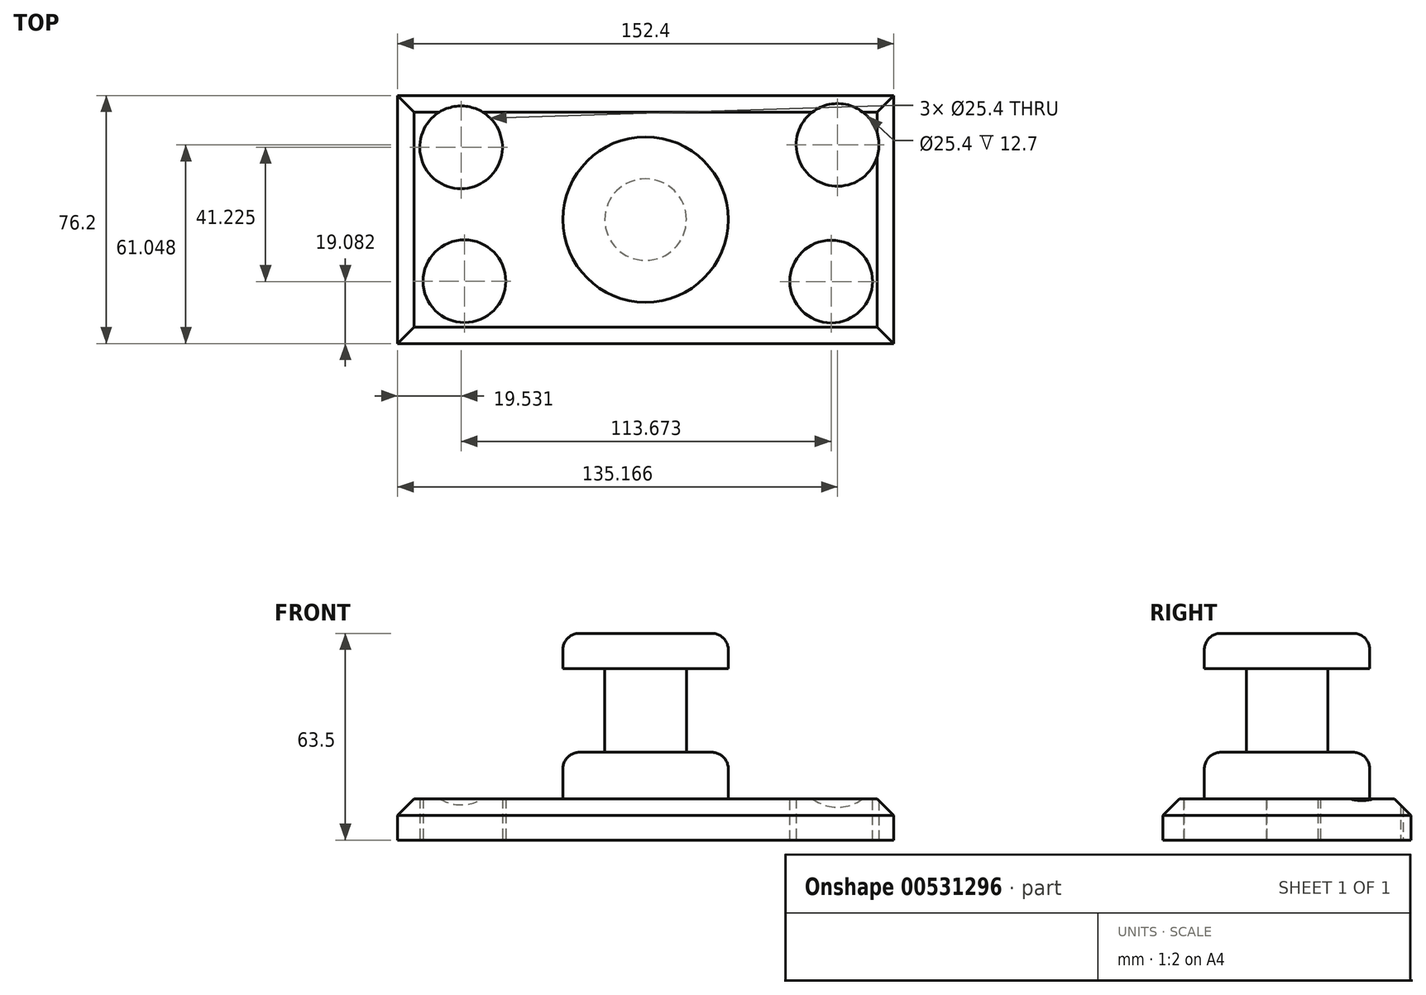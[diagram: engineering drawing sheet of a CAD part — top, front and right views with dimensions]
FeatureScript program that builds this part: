
annotation { "Feature Type Name" : "Feature", "Feature Type Description" : "" }
export const myFeature = defineFeature(function(context is Context, id is Id, definition is map)
    precondition{}
    {
        {
            var Q0;
            Q0=qCreatedBy(makeId("Top.planeOp"),FACE);
            var sketch = newSketch(context, id + "F0", { "sketchPlane" : qUnion([Q0])});
            skLineSegment(sketch, "E0.bottom", {"start": v(-76.2, 38.1) * mm, "end": v(76.2, 38.1) * mm});
            skLineSegment(sketch, "E0.top", {"start": v(-76.2, -38.1) * mm, "end": v(76.2, -38.1) * mm});
            skLineSegment(sketch, "E0.left", {"start": v(-76.2, 38.1) * mm, "end": v(-76.2, -38.1) * mm});
            skLineSegment(sketch, "E0.right", {"start": v(76.2, 38.1) * mm, "end": v(76.2, -38.1) * mm});
            skPoint(sketch, "E0.middle", {"position": v(0, 0) * mm});
            skSolve(sketch);
        }
        {
            var Q0;
            Q0=makeQuery(id+"F0.imprint","IMPRINT",FACE,{"disambiguationData":[TD([[makeQuery(id+"F0.imprint","IMPRINT",EDGE,{"derivedFrom":sQuery(id+"F0.wireOp",EDGE,"E0.bottom")}),-1.0]])]});
            extrude(context, id + "F1", {"entities" : qUnion([Q0]), "depth" : 12.7 * mm, "offsetDistance" : 25.4 * mm});
        }
        {
            var Q0;
            Q0=makeQuery(id+"F1.opExtrude","CAP_FACE",FACE,{"disambiguationData":[OSD([sQuery(id+"F0.wireOp",EDGE,"E0.bottom"),sQuery(id+"F0.wireOp",EDGE,"E0.top"),sQuery(id+"F0.wireOp",EDGE,"E0.left"),sQuery(id+"F0.wireOp",EDGE,"E0.right")])],"isStart":false});
            var sketch = newSketch(context, id + "F2", { "sketchPlane" : qUnion([Q0])});
            skCircle(sketch, "E1", {"center": v(57, -19.02) * mm, "radius": 12.7 * mm});
            skSolve(sketch);
        }
        {
            var Q0;
            Q0 = qSketchRegion(id + "F2", true);
            extrude(context, id + "F3", {"entities" : qUnion([Q0]), "operationType" : NewBodyOperationType.REMOVE, "oppositeDirection" : true, "depth" : 12.7 * mm, "offsetDistance" : 25.4 * mm});
        }
        {
            var Q0;
            Q0=qCreatedBy(makeId("Top.planeOp"),FACE);
            var sketch = newSketch(context, id + "F4", { "sketchPlane" : qUnion([Q0])});
            skCircle(sketch, "E2", {"center": v(-55.63, -18.93) * mm, "radius": 12.7 * mm});
            skSolve(sketch);
        }
        {
            var Q0;
            Q0 = qSketchRegion(id + "F4", true);
            extrude(context, id + "F5", {"entities" : qUnion([Q0]), "operationType" : NewBodyOperationType.REMOVE, "depth" : 12.7 * mm, "offsetDistance" : 25.4 * mm});
        }
        {
            var Q0;
            Q0=qCreatedBy(makeId("Top.planeOp"),FACE);
            var sketch = newSketch(context, id + "F6", { "sketchPlane" : qUnion([Q0])});
            skCircle(sketch, "E3", {"center": v(-56.67, 22.2) * mm, "radius": 12.7 * mm});
            skCircle(sketch, "E4", {"center": v(58.97, 22.95) * mm, "radius": 12.7 * mm});
            skSolve(sketch);
        }
        {
            var Q0;
            Q0 = qSketchRegion(id + "F6", true);
            extrude(context, id + "F7", {"entities" : qUnion([Q0]), "operationType" : NewBodyOperationType.REMOVE, "depth" : 12.7 * mm, "offsetDistance" : 25.4 * mm});
        }
        {
            var Q0;
            Q0=qCreatedBy(makeId("Front.planeOp"),FACE);
            var sketch = newSketch(context, id + "F8", { "sketchPlane" : qUnion([Q0])});
            skLineSegment(sketch, "E5.bottom", {"start": v(0, 12.7) * mm, "end": v(25.4, 12.7) * mm});
            skLineSegment(sketch, "E5.top", {"start": v(0, 63.5) * mm, "end": v(25.4, 63.5) * mm});
            skLineSegment(sketch, "E5.left", {"start": v(0, 12.7) * mm, "end": v(0, 63.5) * mm});
            skLineSegment(sketch, "E5.right", {"start": v(25.4, 12.7) * mm, "end": v(25.4, 63.5) * mm});
            skSolve(sketch);
        }
        {
            var Q0;
            Q0=makeQuery(id+"F8.imprint","IMPRINT",FACE,{"disambiguationData":[TD([[makeQuery(id+"F8.imprint","IMPRINT",EDGE,{"derivedFrom":sQuery(id+"F8.wireOp",EDGE,"E5.bottom")}),1.0]])]});
            var Q1;
            Q1=sQuery(id+"F8.wireOp",EDGE,"E5.left");
            revolve(context, id + "F9", {"operationType" : NewBodyOperationType.ADD, "entities" : qUnion([Q0]), "axis" : qUnion([Q1]), "revolveType" : RevolveType.FULL});
        }
        {
            var Q0;
            Q0=qCreatedBy(makeId("Front.planeOp"),FACE);
            var sketch = newSketch(context, id + "F10", { "sketchPlane" : qUnion([Q0])});
            skLineSegment(sketch, "E6", {"start": v(0, 0) * mm, "end": v(0, 63.4) * mm});
            skSolve(sketch);
        }
        {
            var Q0;
            Q0=qCreatedBy(makeId("Front.planeOp"),FACE);
            var sketch = newSketch(context, id + "F11", { "sketchPlane" : qUnion([Q0])});
            skLineSegment(sketch, "E7.bottom", {"start": v(-35.27, 52.61) * mm, "end": v(-12.53, 52.61) * mm});
            skLineSegment(sketch, "E7.top", {"start": v(-35.27, 26.96) * mm, "end": v(-12.53, 26.96) * mm});
            skLineSegment(sketch, "E7.left", {"start": v(-35.27, 52.61) * mm, "end": v(-35.27, 26.96) * mm});
            skLineSegment(sketch, "E7.right", {"start": v(-12.53, 52.61) * mm, "end": v(-12.53, 26.96) * mm});
            skSolve(sketch);
        }
        {
            var Q0;
            Q0=makeQuery(id+"F11.imprint","IMPRINT",FACE,{"disambiguationData":[TD([[makeQuery(id+"F11.imprint","IMPRINT",EDGE,{"derivedFrom":sQuery(id+"F11.wireOp",EDGE,"E7.bottom")}),-1.0]])]});
            var Q1;
            Q1=sQuery(id+"F10.wireOp",EDGE,"E6");
            revolve(context, id + "F12", {"operationType" : NewBodyOperationType.REMOVE, "entities" : qUnion([Q0]), "axis" : qUnion([Q1]), "revolveType" : RevolveType.FULL, "oppositeDirection" : true});
        }
        {
            var Q0;
            Q0=makeQuery(id+"F9.opRevolve","SWEPT_EDGE",EDGE,{"disambiguationData":[OSD([sQuery(id+"F8.wireOp",EDGE,"E5.top"),sQuery(id+"F8.wireOp",EDGE,"E5.right")])]});
            var Q1;
            Q1=makeQuery(id+"F12.boolean.opBoolean","INTERSECT",EDGE,{"derivedFrom":[makeQuery(id+"F9.opRevolve","SWEPT_FACE",FACE,{"disambiguationData":[OSD([sQuery(id+"F8.wireOp",EDGE,"E5.right")])]}),makeQuery(id+"F12.opRevolve","SWEPT_FACE",FACE,{"disambiguationData":[OSD([sQuery(id+"F11.wireOp",EDGE,"E7.top")])]})]});
            var Q2;
            Q2=makeQuery(id+"F9.opRevolve","SWEPT_EDGE",EDGE,{"disambiguationData":[OSD([sQuery(id+"F8.wireOp",EDGE,"E5.bottom"),sQuery(id+"F8.wireOp",EDGE,"E5.right")])]});
            fillet(context, id + "F13", {"entities" : qUnion([Q0, Q1, Q2]), "radius" : 5.08 * mm, "tangentPropagation" : true, "allowEdgeOverflow" : false});
        }
        {
            var Q0;
            Q0=makeQuery(id+"F1.opExtrude","CAP_EDGE",EDGE,{"disambiguationData":[OSD([sQuery(id+"F0.wireOp",EDGE,"E0.top")])],"isStart":false});
            var Q1;
            Q1=makeQuery(id+"F1.opExtrude","CAP_EDGE",EDGE,{"disambiguationData":[OSD([sQuery(id+"F0.wireOp",EDGE,"E0.left")])],"isStart":false});
            var Q2;
            Q2=makeQuery(id+"F1.opExtrude","CAP_EDGE",EDGE,{"disambiguationData":[OSD([sQuery(id+"F0.wireOp",EDGE,"E0.bottom")])],"isStart":false});
            var Q3;
            Q3=makeQuery(id+"F1.opExtrude","CAP_EDGE",EDGE,{"disambiguationData":[OSD([sQuery(id+"F0.wireOp",EDGE,"E0.right")])],"isStart":false});
            chamfer(context, id + "F14", {"entities" : qUnion([Q0, Q1, Q2, Q3]), "width" : 5.08 * mm, "tangentPropagation" : true});
        }
    });
